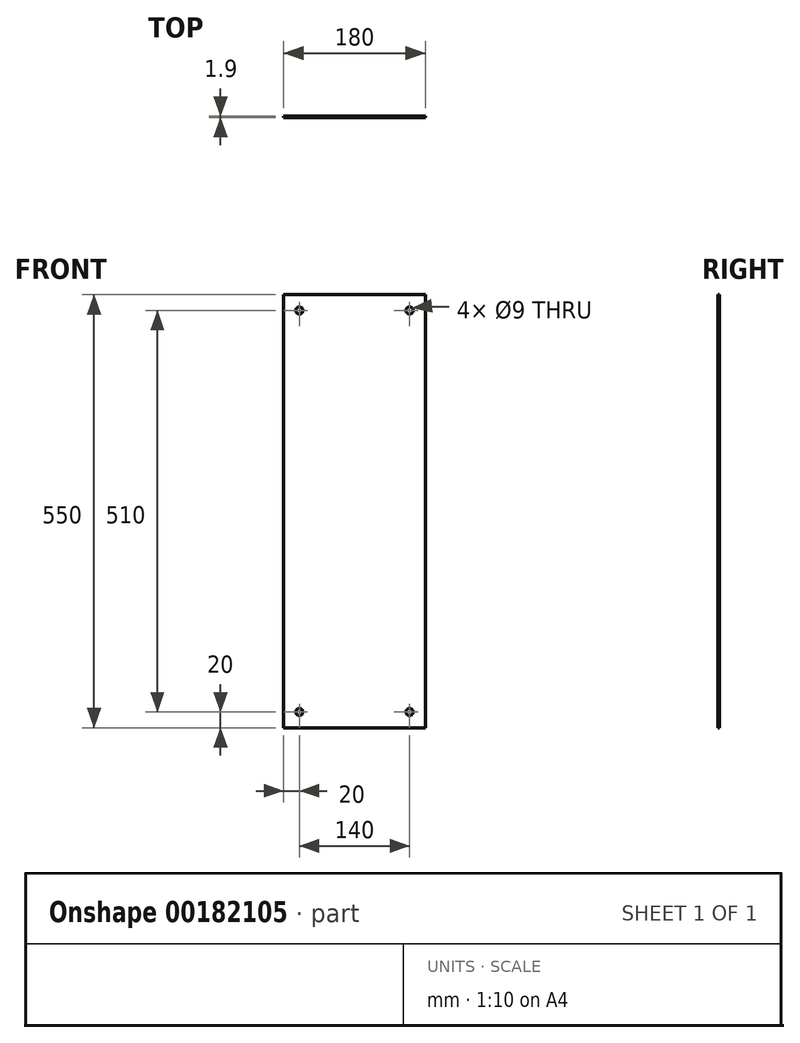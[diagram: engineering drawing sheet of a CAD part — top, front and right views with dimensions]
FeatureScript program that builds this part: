
annotation { "Feature Type Name" : "Feature", "Feature Type Description" : "" }
export const myFeature = defineFeature(function(context is Context, id is Id, definition is map)
    precondition{}
    {
        {
            var Q0;
            Q0=qCreatedBy(makeId("Front.planeOp"),FACE);
            var sketch = newSketch(context, id + "F0", { "sketchPlane" : qUnion([Q0])});
            skLineSegment(sketch, "E0.bottom", {"start": v(0, 275) * mm, "end": v(180, 275) * mm});
            skLineSegment(sketch, "E0.top", {"start": v(0, -275) * mm, "end": v(180, -275) * mm});
            skLineSegment(sketch, "E0.left", {"start": v(0, 275) * mm, "end": v(0, -275) * mm});
            skLineSegment(sketch, "E0.right", {"start": v(180, 275) * mm, "end": v(180, -275) * mm});
            skCircle(sketch, "E1", {"center": v(20, 255) * mm, "radius": 4.5 * mm});
            skCircle(sketch, "E2", {"center": v(160, 255) * mm, "radius": 4.5 * mm});
            skCircle(sketch, "E3", {"center": v(20, -255) * mm, "radius": 4.5 * mm});
            skCircle(sketch, "E4", {"center": v(160, -255) * mm, "radius": 4.5 * mm});
            skSolve(sketch);
        }
        {
            var Q0;
            Q0 = qSketchRegion(id + "F0", true);
            extrude(context, id + "F1", {"entities" : qUnion([Q0]), "depth" : 1.9 * mm});
        }
    });
